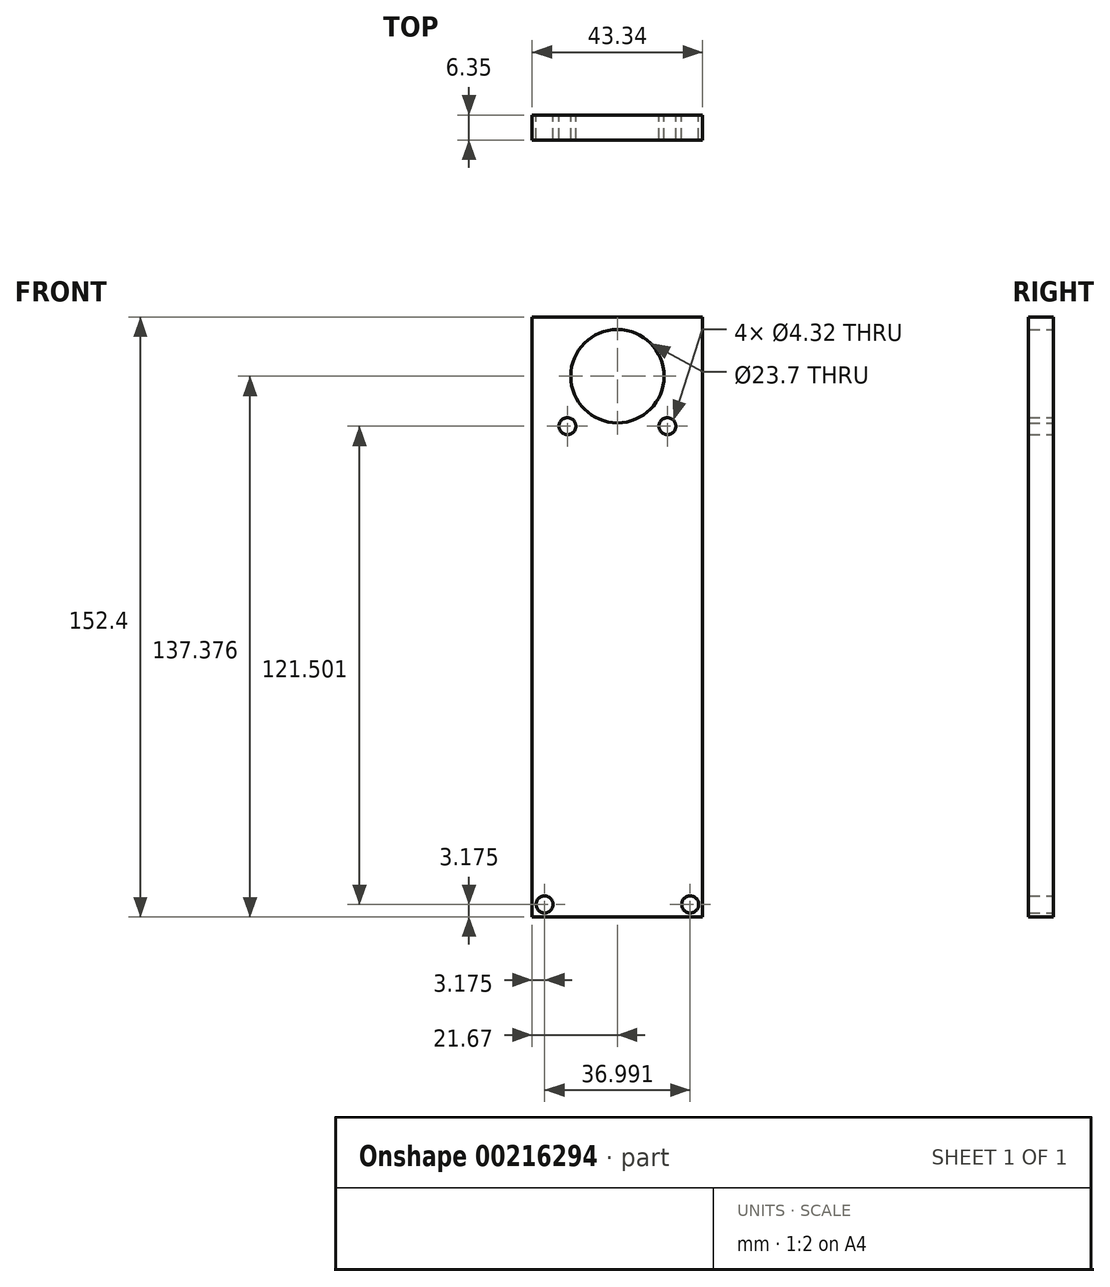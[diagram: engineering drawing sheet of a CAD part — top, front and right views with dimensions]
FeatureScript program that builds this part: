
annotation { "Feature Type Name" : "Feature", "Feature Type Description" : "" }
export const myFeature = defineFeature(function(context is Context, id is Id, definition is map)
    precondition{}
    {
        {
            var Q0;
            Q0=qCreatedBy(makeId("Front.planeOp"),FACE);
            var sketch = newSketch(context, id + "F0", { "sketchPlane" : qUnion([Q0])});
            skLineSegment(sketch, "E0.bottom", {"start": v(21.67, -76.2) * mm, "end": v(-21.67, -76.2) * mm});
            skLineSegment(sketch, "E0.top", {"start": v(21.67, 76.2) * mm, "end": v(-21.67, 76.2) * mm});
            skLineSegment(sketch, "E0.left", {"start": v(21.67, -76.2) * mm, "end": v(21.67, 76.2) * mm});
            skLineSegment(sketch, "E0.right", {"start": v(-21.67, -76.2) * mm, "end": v(-21.67, 76.2) * mm});
            skPoint(sketch, "E0.middle", {"position": v(0, 0) * mm});
            skCircle(sketch, "E1", {"center": v(18.5, -73.03) * mm, "radius": 2.16 * mm});
            skCircle(sketch, "E2.MirrorC", {"center": v(-18.5, -73.03) * mm, "radius": 2.16 * mm});
            skCircle(sketch, "E3", {"center": v(0, 61.18) * mm, "radius": 11.85 * mm});
            skCircle(sketch, "E4", {"center": v(-12.7, 48.48) * mm, "radius": 2.16 * mm});
            skCircle(sketch, "E5.MirrorC", {"center": v(12.7, 48.48) * mm, "radius": 2.16 * mm});
            skSolve(sketch);
        }
        {
            var Q0;
            Q0 = qSketchRegion(id + "F0", true);
            extrude(context, id + "F1", {"entities" : qUnion([Q0]), "depth" : 6.35 * mm});
        }
    });
